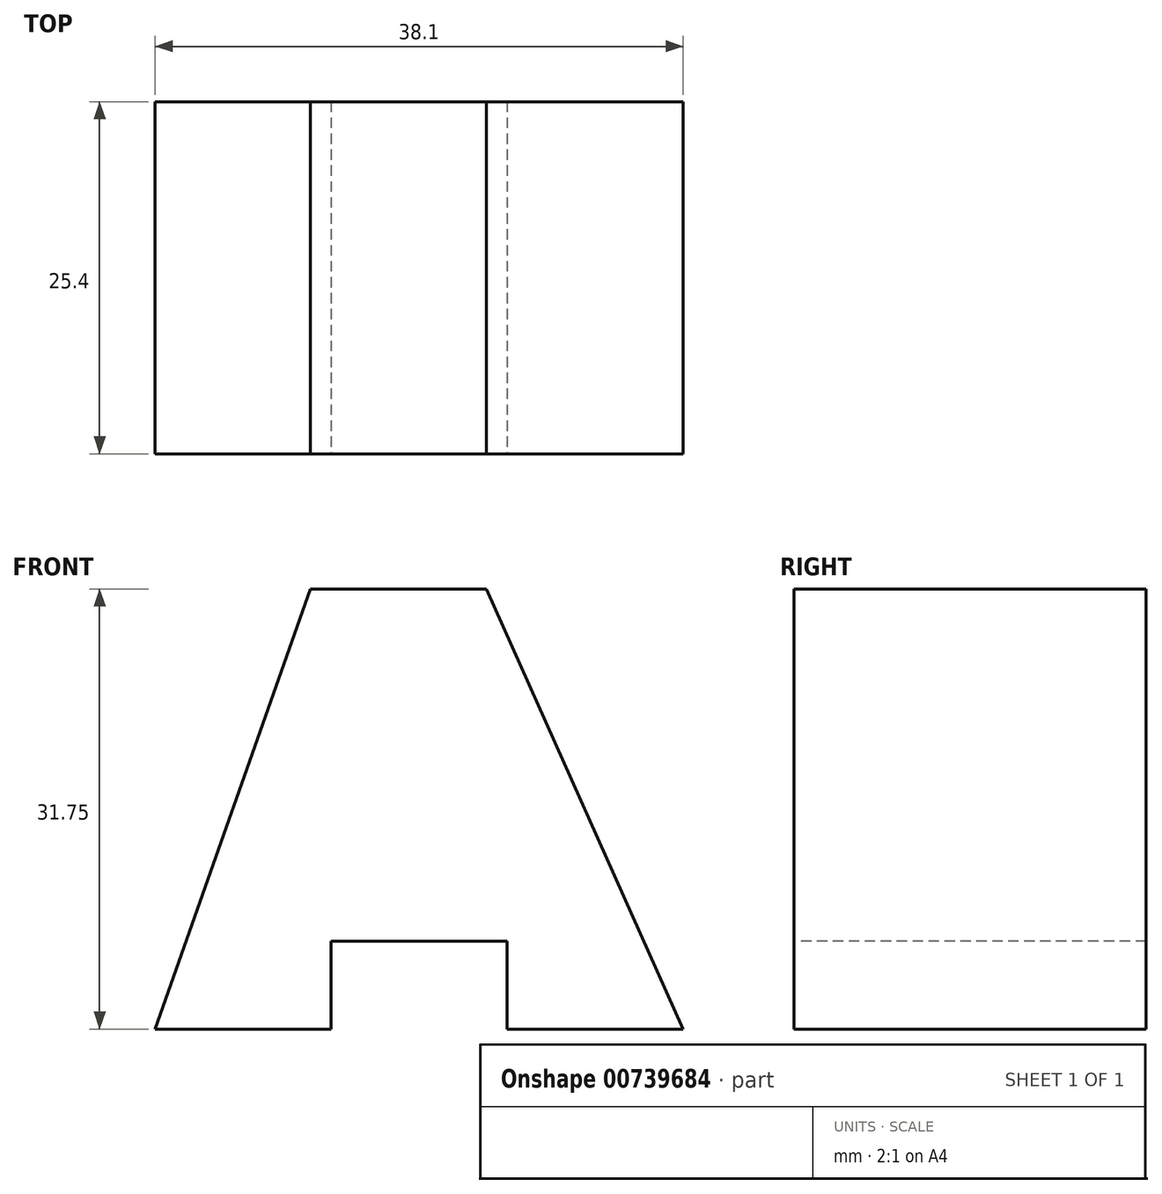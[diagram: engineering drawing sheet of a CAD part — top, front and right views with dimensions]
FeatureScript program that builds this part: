
annotation { "Feature Type Name" : "Feature", "Feature Type Description" : "" }
export const myFeature = defineFeature(function(context is Context, id is Id, definition is map)
    precondition{}
    {
        {
            var Q0;
            Q0=qCreatedBy(makeId("Front.planeOp"),FACE);
            var sketch = newSketch(context, id + "F0", { "sketchPlane" : qUnion([Q0])});
            skLineSegment(sketch, "E0.bottom", {"start": v(0, 0) * mm, "end": v(38.1, 0) * mm});
            skLineSegment(sketch, "E0.top", {"start": v(0, 31.75) * mm, "end": v(38.1, 31.75) * mm});
            skLineSegment(sketch, "E0.left", {"start": v(0, 0) * mm, "end": v(0, 31.75) * mm});
            skLineSegment(sketch, "E0.right", {"start": v(38.1, 0) * mm, "end": v(38.1, 31.75) * mm});
            skSolve(sketch);
        }
        {
            var Q0;
            Q0 = qSketchRegion(id + "F0", true);
            extrude(context, id + "F1", {"entities" : qUnion([Q0]), "depth" : 25.4 * mm, "offsetDistance" : 25.4 * mm});
        }
        {
            var Q0;
            Q0=makeQuery(id+"F1.opExtrude","CAP_FACE",FACE,{"disambiguationData":[OSD([sQuery(id+"F0.wireOp",EDGE,"E0.bottom"),sQuery(id+"F0.wireOp",EDGE,"E0.top"),sQuery(id+"F0.wireOp",EDGE,"E0.left"),sQuery(id+"F0.wireOp",EDGE,"E0.right")])],"isStart":false});
            var sketch = newSketch(context, id + "F2", { "sketchPlane" : qUnion([Q0])});
            skLineSegment(sketch, "E1", {"start": v(23.9, 31.75) * mm, "end": v(38.1, 0) * mm});
            skLineSegment(sketch, "E2", {"start": v(38.1, 0) * mm, "end": v(38.1, 31.75) * mm});
            skLineSegment(sketch, "E3", {"start": v(38.1, 31.75) * mm, "end": v(23.9, 31.75) * mm});
            skLineSegment(sketch, "E4", {"start": v(11.2, 31.75) * mm, "end": v(0, 0) * mm});
            skLineSegment(sketch, "E5", {"start": v(0, 0) * mm, "end": v(0, 31.75) * mm});
            skLineSegment(sketch, "E6", {"start": v(0, 31.75) * mm, "end": v(11.2, 31.75) * mm});
            skSolve(sketch);
        }
        {
            var Q0;
            Q0 = qSketchRegion(id + "F2", true);
            extrude(context, id + "F3", {"entities" : qUnion([Q0]), "operationType" : NewBodyOperationType.REMOVE, "oppositeDirection" : true, "depth" : 25.4 * mm, "offsetDistance" : 25.4 * mm});
        }
        {
            var Q0;
            Q0=makeQuery(id+"F1.opExtrude","CAP_FACE",FACE,{"disambiguationData":[OSD([sQuery(id+"F0.wireOp",EDGE,"E0.bottom"),sQuery(id+"F0.wireOp",EDGE,"E0.top"),sQuery(id+"F0.wireOp",EDGE,"E0.left"),sQuery(id+"F0.wireOp",EDGE,"E0.right")])],"isStart":false});
            var sketch = newSketch(context, id + "F4", { "sketchPlane" : qUnion([Q0])});
            skLineSegment(sketch, "E7.bottom", {"start": v(12.7, 0) * mm, "end": v(25.4, 0) * mm});
            skLineSegment(sketch, "E7.top", {"start": v(12.7, 6.35) * mm, "end": v(25.4, 6.35) * mm});
            skLineSegment(sketch, "E7.left", {"start": v(12.7, 0) * mm, "end": v(12.7, 6.35) * mm});
            skLineSegment(sketch, "E7.right", {"start": v(25.4, 0) * mm, "end": v(25.4, 6.35) * mm});
            skSolve(sketch);
        }
        {
            var Q0;
            Q0 = qSketchRegion(id + "F4", true);
            extrude(context, id + "F5", {"entities" : qUnion([Q0]), "operationType" : NewBodyOperationType.REMOVE, "oppositeDirection" : true, "depth" : 25.4 * mm, "offsetDistance" : 25.4 * mm});
        }
    });
